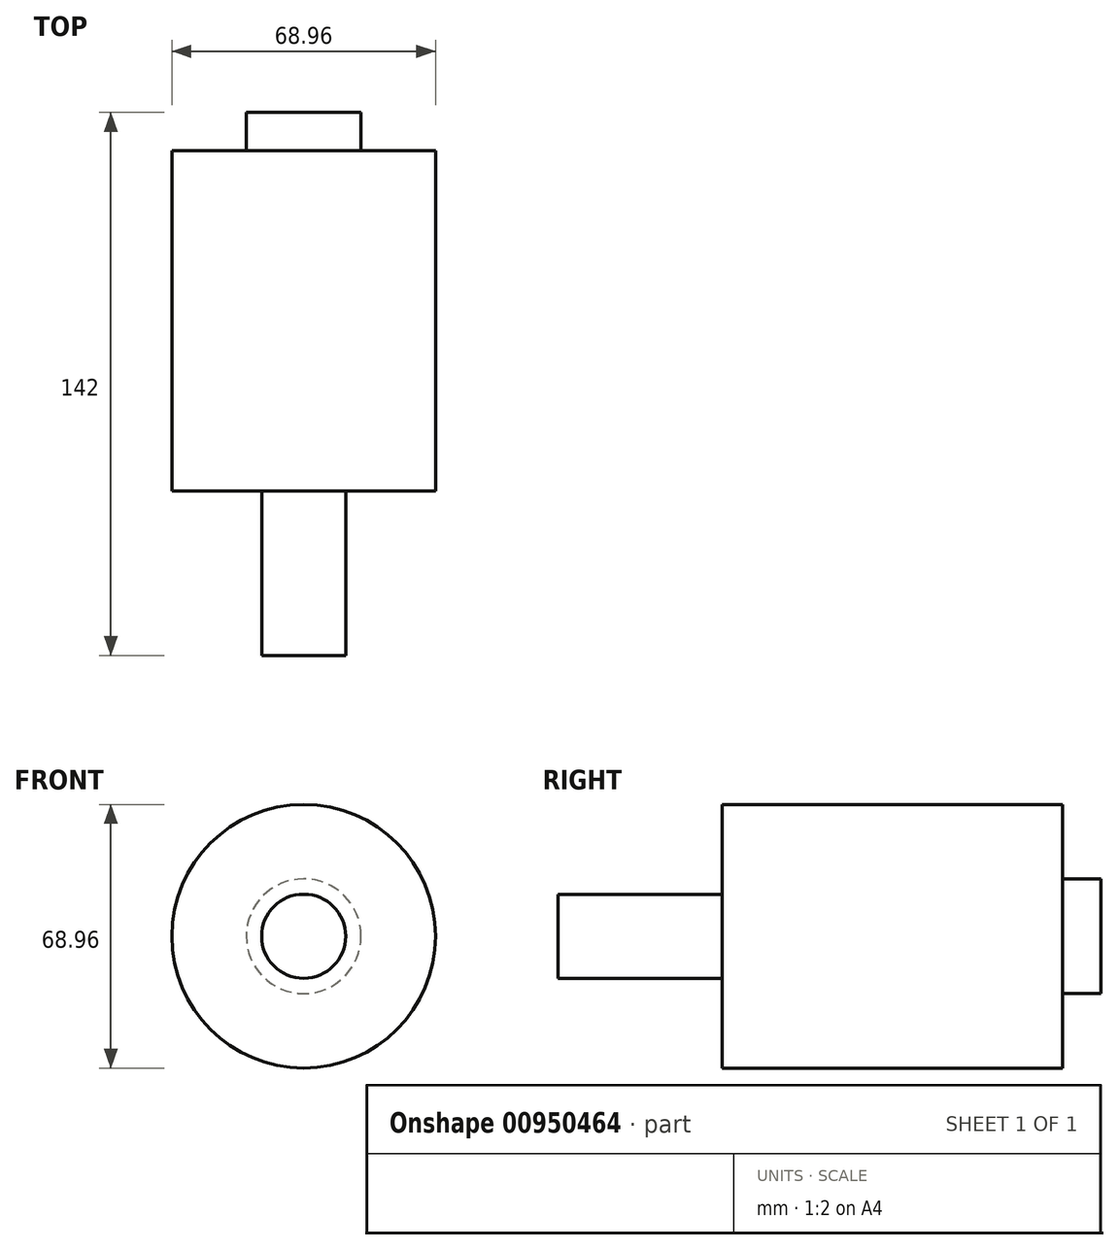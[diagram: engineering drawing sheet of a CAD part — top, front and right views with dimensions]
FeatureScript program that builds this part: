
annotation { "Feature Type Name" : "Feature", "Feature Type Description" : "" }
export const myFeature = defineFeature(function(context is Context, id is Id, definition is map)
    precondition{}
    {
        {
            var Q0;
            Q0=qCreatedBy(makeId("Front.planeOp"),FACE);
            var sketch = newSketch(context, id + "F0", { "sketchPlane" : qUnion([Q0])});
            skCircle(sketch, "E0", {"center": v(0, 0) * mm, "radius": 34.48 * mm});
            skSolve(sketch);
        }
        {
            var Q0;
            Q0=qSketchRegion(id+"F0",true);
            extrude(context, id + "F1", {"entities" : qUnion([Q0]), "depth" : 89 * mm, "offsetDistance" : 25 * mm});
        }
        {
            var Q0;
            Q0=makeQuery(id+"F1.opExtrude","CAP_FACE",FACE,{"disambiguationData":[OSD([sQuery(id+"F0.wireOp",EDGE,"E0")])],"isStart":false});
            var sketch = newSketch(context, id + "F2", { "sketchPlane" : qUnion([Q0])});
            skCircle(sketch, "E1", {"center": v(0, 0) * mm, "radius": 11 * mm});
            skSolve(sketch);
        }
        {
            var Q0;
            Q0=qSketchRegion(id+"F2",true);
            extrude(context, id + "F3", {"entities" : qUnion([Q0]), "operationType" : NewBodyOperationType.ADD, "depth" : 43 * mm, "offsetDistance" : 25 * mm});
        }
        {
            var Q0;
            Q0=makeQuery(id+"F1.opExtrude","CAP_FACE",FACE,{"disambiguationData":[OSD([sQuery(id+"F0.wireOp",EDGE,"E0")])],"isStart":true});
            var sketch = newSketch(context, id + "F4", { "sketchPlane" : qUnion([Q0])});
            skCircle(sketch, "E2", {"center": v(0, 0) * mm, "radius": 15 * mm});
            skSolve(sketch);
        }
        {
            var Q0;
            Q0=qSketchRegion(id+"F4",true);
            extrude(context, id + "F5", {"entities" : qUnion([Q0]), "operationType" : NewBodyOperationType.ADD, "depth" : 10 * mm, "offsetDistance" : 25 * mm});
        }
    });
